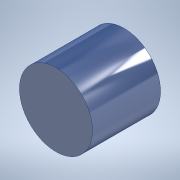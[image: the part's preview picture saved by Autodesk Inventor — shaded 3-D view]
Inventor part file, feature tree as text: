
AUTODESK INVENTOR PART (.ipt)
format: ipt  version: 2020 (Build 240168000, 168)  size: 109,568 bytes
history: native  units: mm
features: extrude x1, sketch x1
ambient origin geometry x8: Origin, YZ Plane, XZ Plane, XY Plane, X Axis, Y Axis, Z Axis, Center Point
bodies: Solid1 (feature_tree)
feature tree (2):
  extrude  "Extrusion1"  Depth=70.0mm TaperAngle=0.0deg
  sketch  "Sketch1"  dims[d0=75.0mm d1=70.0mm d2=0.0mm]
